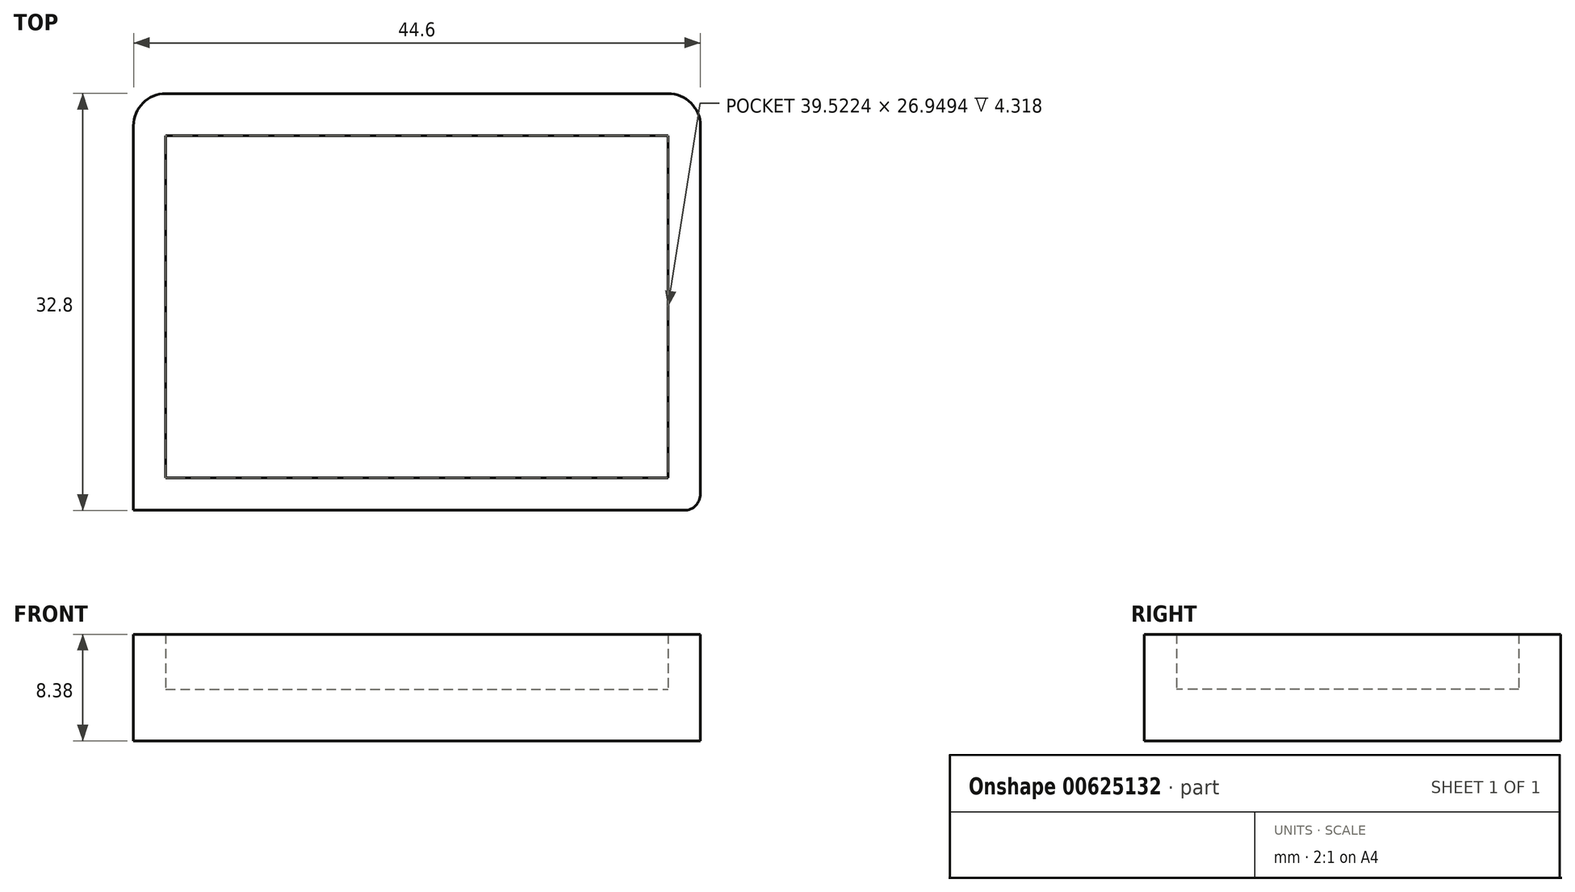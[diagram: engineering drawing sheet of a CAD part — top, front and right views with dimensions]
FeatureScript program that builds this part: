
annotation { "Feature Type Name" : "Feature", "Feature Type Description" : "" }
export const myFeature = defineFeature(function(context is Context, id is Id, definition is map)
    precondition{}
    {
        {
            var Q0;
            Q0=qCreatedBy(makeId("Top.planeOp"),FACE);
            var sketch = newSketch(context, id + "F0", { "sketchPlane" : qUnion([Q0])});
            skLineSegment(sketch, "E0.bottom", {"start": v(-19.43, 11.75) * mm, "end": v(20.09, 11.75) * mm});
            skLineSegment(sketch, "E0.top", {"start": v(-21.97, -21.05) * mm, "end": v(21.36, -21.05) * mm});
            skLineSegment(sketch, "E0.left", {"start": v(-21.97, 9.2) * mm, "end": v(-21.97, -21.05) * mm});
            skLineSegment(sketch, "E0.right", {"start": v(22.63, 9.2) * mm, "end": v(22.63, -19.78) * mm});
            skPoint(sketch, "E1.visualSharp", {"position": v(-21.97, 11.75) * mm});
            skArc(sketch, "E1.filletArc", {"start": v(-19.43, 11.75) * mm, "mid": v(-21.23, 11) * mm, "end": v(-21.97, 9.2) * mm});
            skPoint(sketch, "E2.visualSharp", {"position": v(22.63, 11.75) * mm});
            skArc(sketch, "E2.filletArc", {"start": v(22.63, 9.2) * mm, "mid": v(21.88, 11) * mm, "end": v(20.09, 11.75) * mm});
            skPoint(sketch, "E3.visualSharp", {"position": v(22.63, -21.05) * mm});
            skArc(sketch, "E3.filletArc", {"start": v(21.36, -21.05) * mm, "mid": v(22.26, -20.67) * mm, "end": v(22.63, -19.78) * mm});
            skLineSegment(sketch, "E4.0", {"start": v(-19.43, 8.44) * mm, "end": v(20.09, 8.44) * mm});
            skLineSegment(sketch, "E5", {"start": v(20.09, 8.44) * mm, "end": v(20.09, -18.5) * mm});
            skLineSegment(sketch, "E6", {"start": v(-19.43, -18.5) * mm, "end": v(20.09, -18.5) * mm});
            skLineSegment(sketch, "E7", {"start": v(-19.43, 8.44) * mm, "end": v(-19.43, -18.5) * mm});
            skLineSegment(sketch, "E8", {"start": v(22.63, -12.86) * mm, "end": v(44.41, -12.86) * mm});
            skLineSegment(sketch, "E9", {"start": v(44.41, -12.86) * mm, "end": v(44.41, 3.46) * mm});
            skLineSegment(sketch, "E10", {"start": v(44.41, 3.46) * mm, "end": v(22.63, 3.46) * mm});
            skLineSegment(sketch, "E11", {"start": v(-16.08, 11.75) * mm, "end": v(-16.08, 16.3) * mm});
            skLineSegment(sketch, "E12", {"start": v(-16.08, 16.3) * mm, "end": v(-10.44, 16.3) * mm});
            skLineSegment(sketch, "E13", {"start": v(-10.44, 16.3) * mm, "end": v(-10.44, 11.75) * mm});
            skSolve(sketch);
        }
        {
            var Q0;
            Q0=makeQuery(id+"F0.imprint","IMPRINT",FACE,{"disambiguationData":[TD([[makeQuery(id+"F0.imprint","IMPRINT",EDGE,{"derivedFrom":sQuery(id+"F0.wireOp",EDGE,"E0.bottom")}),-1.0]])]});
            extrude(context, id + "F1", {"entities" : qUnion([Q0]), "depth" : 8.38 * mm, "offsetDistance" : 25.4 * mm});
        }
        {
            var Q0;
            Q0=makeQuery(id+"F0.imprint","IMPRINT",FACE,{"disambiguationData":[TD([[makeQuery(id+"F0.imprint","IMPRINT",EDGE,{"derivedFrom":sQuery(id+"F0.wireOp",EDGE,"E4.0")}),-1.0]])]});
            extrude(context, id + "F2", {"entities" : qUnion([Q0]), "operationType" : NewBodyOperationType.ADD, "depth" : 4.06 * mm, "offsetDistance" : 25.4 * mm});
        }
    });
